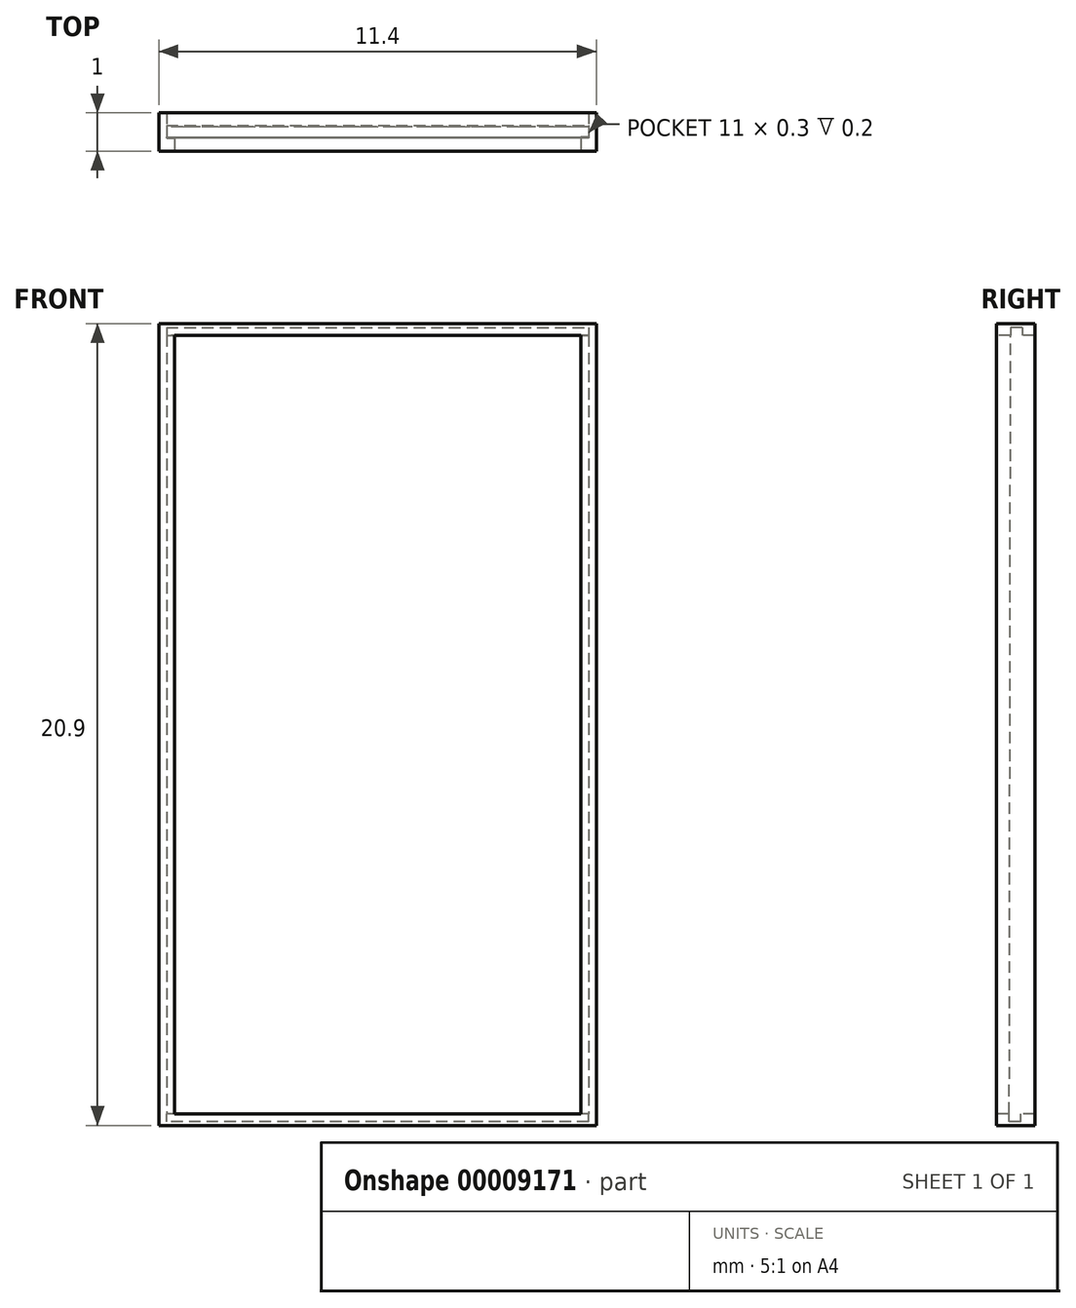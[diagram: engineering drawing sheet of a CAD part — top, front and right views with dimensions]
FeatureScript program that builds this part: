
annotation { "Feature Type Name" : "Feature", "Feature Type Description" : "" }
export const myFeature = defineFeature(function(context is Context, id is Id, definition is map)
    precondition{}
    {
        {
            var Q0;
            Q0=qCreatedBy(makeId("Front.planeOp"),FACE);
            var sketch = newSketch(context, id + "F0", { "sketchPlane" : qUnion([Q0])});
            skLineSegment(sketch, "E0.rect.bottom", {"start": v(5.7, 10.45) * mm, "end": v(-5.7, 10.45) * mm});
            skLineSegment(sketch, "E0.rect.top", {"start": v(5.7, -10.45) * mm, "end": v(-5.7, -10.45) * mm});
            skLineSegment(sketch, "E0.rect.left", {"start": v(5.7, 10.45) * mm, "end": v(5.7, -10.45) * mm});
            skLineSegment(sketch, "E0.rect.right", {"start": v(-5.7, 10.45) * mm, "end": v(-5.7, -10.45) * mm});
            skPoint(sketch, "E0.rect.middle", {"position": v(0, 0) * mm});
            skSolve(sketch);
        }
        {
            var Q0;
            Q0 = qSketchRegion(id + "F0", true);
            extrude(context, id + "F1", {"entities" : qUnion([Q0]), "oppositeDirection" : true, "depth" : 1 * mm});
        }
        {
            var Q0;
            Q0=makeQuery(id+"F1.opExtrude","CAP_FACE",FACE,{"disambiguationData":[OSD([sQuery(id+"F0.wireOp",EDGE,"E0.rect.bottom"),sQuery(id+"F0.wireOp",EDGE,"E0.rect.top"),sQuery(id+"F0.wireOp",EDGE,"E0.rect.left"),sQuery(id+"F0.wireOp",EDGE,"E0.rect.right")])],"isStart":true});
            var sketch = newSketch(context, id + "F2", { "sketchPlane" : qUnion([Q0])});
            skLineSegment(sketch, "E1.rect.bottom", {"start": v(5.3, 10.15) * mm, "end": v(-5.3, 10.15) * mm});
            skLineSegment(sketch, "E1.rect.top", {"start": v(5.3, -10.15) * mm, "end": v(-5.3, -10.15) * mm});
            skLineSegment(sketch, "E1.rect.left", {"start": v(5.3, 10.15) * mm, "end": v(5.3, -10.15) * mm});
            skLineSegment(sketch, "E1.rect.right", {"start": v(-5.3, 10.15) * mm, "end": v(-5.3, -10.15) * mm});
            skPoint(sketch, "E1.rect.middle", {"position": v(0, 0) * mm});
            skSolve(sketch);
        }
        {
            var Q0;
            Q0 = qSketchRegion(id + "F2", true);
            extrude(context, id + "F3", {"entities" : qUnion([Q0]), "operationType" : NewBodyOperationType.REMOVE, "oppositeDirection" : true, "depth" : 25 * mm});
        }
        {
            var Q0;
            Q0=makeQuery(id+"F3.boolean.opBoolean","COPY",FACE,{"derivedFrom":makeQuery(id+"F3.opExtrude","SWEPT_FACE",FACE,{"disambiguationData":[OSD([sQuery(id+"F2.wireOp",EDGE,"E1.rect.top")])]})});
            var sketch = newSketch(context, id + "F4", { "sketchPlane" : qUnion([Q0])});
            skLineSegment(sketch, "E2.rect.bottom", {"start": v(5.3, 0.33) * mm, "end": v(-5.3, 0.33) * mm});
            skLineSegment(sketch, "E2.rect.top", {"start": v(5.3, 0.63) * mm, "end": v(-5.3, 0.63) * mm});
            skLineSegment(sketch, "E2.rect.left", {"start": v(5.3, 0.33) * mm, "end": v(5.3, 0.63) * mm});
            skLineSegment(sketch, "E2.rect.right", {"start": v(-5.3, 0.33) * mm, "end": v(-5.3, 0.63) * mm});
            skPoint(sketch, "E2.rect.middle", {"position": v(0, 0.48) * mm});
            skSolve(sketch);
        }
        {
            var Q0;
            Q0 = qSketchRegion(id + "F4", true);
            extrude(context, id + "F5", {"entities" : qUnion([Q0]), "operationType" : NewBodyOperationType.REMOVE, "oppositeDirection" : true, "depth" : 0.2 * mm});
        }
        {
            var Q0;
            Q0=makeQuery(id+"F3.boolean.opBoolean","COPY",FACE,{"derivedFrom":makeQuery(id+"F3.opExtrude","SWEPT_FACE",FACE,{"disambiguationData":[OSD([sQuery(id+"F2.wireOp",EDGE,"E1.rect.bottom")])]})});
            var sketch = newSketch(context, id + "F6", { "sketchPlane" : qUnion([Q0])});
            skLineSegment(sketch, "E3.rect.bottom", {"start": v(-5.3, -0.37) * mm, "end": v(5.3, -0.37) * mm});
            skLineSegment(sketch, "E3.rect.top", {"start": v(-5.3, -0.67) * mm, "end": v(5.3, -0.67) * mm});
            skLineSegment(sketch, "E3.rect.left", {"start": v(-5.3, -0.37) * mm, "end": v(-5.3, -0.67) * mm});
            skLineSegment(sketch, "E3.rect.right", {"start": v(5.3, -0.37) * mm, "end": v(5.3, -0.67) * mm});
            skPoint(sketch, "E3.rect.middle", {"position": v(0, -0.52) * mm});
            skSolve(sketch);
        }
        {
            var Q0;
            Q0 = qSketchRegion(id + "F6", true);
            extrude(context, id + "F7", {"entities" : qUnion([Q0]), "operationType" : NewBodyOperationType.REMOVE, "oppositeDirection" : true, "depth" : 0.2 * mm});
        }
        {
            var Q0;
            Q0=makeQuery(id+"F7.boolean.opBoolean","MERGE",FACE,{"derivedFrom":[makeQuery(id+"F5.boolean.opBoolean","MERGE",FACE,{"derivedFrom":[makeQuery(id+"F3.boolean.opBoolean","COPY",FACE,{"derivedFrom":makeQuery(id+"F3.opExtrude","SWEPT_FACE",FACE,{"disambiguationData":[OSD([sQuery(id+"F2.wireOp",EDGE,"E1.rect.right")])]})}),makeQuery(id+"F5.opExtrude","SWEPT_FACE",FACE,{"disambiguationData":[OSD([sQuery(id+"F4.wireOp",EDGE,"E2.rect.right")])]})]}),makeQuery(id+"F7.opExtrude","SWEPT_FACE",FACE,{"disambiguationData":[OSD([sQuery(id+"F6.wireOp",EDGE,"E3.rect.left")])]})]});
            var sketch = newSketch(context, id + "F8", { "sketchPlane" : qUnion([Q0])});
            skLineSegment(sketch, "E4", {"start": v(0.33, -10.15) * mm, "end": v(0.37, 10.15) * mm});
            skLineSegment(sketch, "E5", {"start": v(0.67, 10.15) * mm, "end": v(0.63, -10.15) * mm});
            skSolve(sketch);
        }
        {
            var Q0;
            Q0=makeQuery(id+"F8.imprint","IMPRINT",FACE,{"disambiguationData":[TD([[makeQuery(id+"F8.imprint","IMPRINT",EDGE,{"derivedFrom":sQuery(id+"F8.wireOp",EDGE,"E4")}),-1.0]])]});
            extrude(context, id + "F9", {"entities" : qUnion([Q0]), "operationType" : NewBodyOperationType.REMOVE, "oppositeDirection" : true, "depth" : 0.2 * mm});
        }
        {
            var Q0;
            Q0=makeQuery(id+"F7.boolean.opBoolean","MERGE",FACE,{"derivedFrom":[makeQuery(id+"F5.boolean.opBoolean","MERGE",FACE,{"derivedFrom":[makeQuery(id+"F3.boolean.opBoolean","COPY",FACE,{"derivedFrom":makeQuery(id+"F3.opExtrude","SWEPT_FACE",FACE,{"disambiguationData":[OSD([sQuery(id+"F2.wireOp",EDGE,"E1.rect.left")])]})}),makeQuery(id+"F5.opExtrude","SWEPT_FACE",FACE,{"disambiguationData":[OSD([sQuery(id+"F4.wireOp",EDGE,"E2.rect.left")])]})]}),makeQuery(id+"F7.opExtrude","SWEPT_FACE",FACE,{"disambiguationData":[OSD([sQuery(id+"F6.wireOp",EDGE,"E3.rect.right")])]})]});
            var sketch = newSketch(context, id + "F10", { "sketchPlane" : qUnion([Q0])});
            skLineSegment(sketch, "E6", {"start": v(-0.33, -10.15) * mm, "end": v(-0.37, 10.15) * mm});
            skLineSegment(sketch, "E7", {"start": v(-0.67, 10.15) * mm, "end": v(-0.63, -10.15) * mm});
            skSolve(sketch);
        }
        {
            var Q0;
            Q0=makeQuery(id+"F10.imprint","IMPRINT",FACE,{"disambiguationData":[TD([[makeQuery(id+"F10.imprint","IMPRINT",EDGE,{"derivedFrom":sQuery(id+"F10.wireOp",EDGE,"E6")}),1.0]])]});
            extrude(context, id + "F11", {"entities" : qUnion([Q0]), "operationType" : NewBodyOperationType.REMOVE, "oppositeDirection" : true, "depth" : 0.2 * mm});
        }
        {
            var Q0;
            {var subQ0=sQuery(id+"F2.wireOp",EDGE,"E1.rect.left");var subQ1=sQuery(id+"F4.wireOp",EDGE,"E2.rect.left");var subQ2=sQuery(id+"F6.wireOp",EDGE,"E3.rect.right");var subQ6=sQuery(id+"F4.wireOp",EDGE,"E2.rect.top");Q0=makeQuery(id+"F11.boolean.opBoolean","SPLIT",FACE,{"disambiguationData":[TD([makeQuery(id+"F5.boolean.opBoolean","COPY",FACE,{"derivedFrom":makeQuery(id+"F5.opExtrude","SWEPT_FACE",FACE,{"disambiguationData":[OSD([subQ6])]})})])],"derivedFrom":makeQuery(id+"F7.boolean.opBoolean","MERGE",FACE,{"derivedFrom":[makeQuery(id+"F5.boolean.opBoolean","MERGE",FACE,{"derivedFrom":[makeQuery(id+"F3.boolean.opBoolean","COPY",FACE,{"derivedFrom":makeQuery(id+"F3.opExtrude","SWEPT_FACE",FACE,{"disambiguationData":[OSD([subQ0])]})}),makeQuery(id+"F5.opExtrude","SWEPT_FACE",FACE,{"disambiguationData":[OSD([subQ1])]})]}),makeQuery(id+"F7.opExtrude","SWEPT_FACE",FACE,{"disambiguationData":[OSD([subQ2])]})]})});}
            extrude(context, id + "F12", {"entities" : qUnion([Q0]), "operationType" : NewBodyOperationType.REMOVE, "oppositeDirection" : true, "depth" : 0.2 * mm});
        }
        {
            var Q0;
            {var subQ0=sQuery(id+"F2.wireOp",EDGE,"E1.rect.right");var subQ1=sQuery(id+"F4.wireOp",EDGE,"E2.rect.right");var subQ2=sQuery(id+"F6.wireOp",EDGE,"E3.rect.left");var subQ6=sQuery(id+"F4.wireOp",EDGE,"E2.rect.top");Q0=makeQuery(id+"F9.boolean.opBoolean","SPLIT",FACE,{"disambiguationData":[TD([makeQuery(id+"F5.boolean.opBoolean","COPY",FACE,{"derivedFrom":makeQuery(id+"F5.opExtrude","SWEPT_FACE",FACE,{"disambiguationData":[OSD([subQ6])]})})])],"derivedFrom":makeQuery(id+"F7.boolean.opBoolean","MERGE",FACE,{"derivedFrom":[makeQuery(id+"F5.boolean.opBoolean","MERGE",FACE,{"derivedFrom":[makeQuery(id+"F3.boolean.opBoolean","COPY",FACE,{"derivedFrom":makeQuery(id+"F3.opExtrude","SWEPT_FACE",FACE,{"disambiguationData":[OSD([subQ0])]})}),makeQuery(id+"F5.opExtrude","SWEPT_FACE",FACE,{"disambiguationData":[OSD([subQ1])]})]}),makeQuery(id+"F7.opExtrude","SWEPT_FACE",FACE,{"disambiguationData":[OSD([subQ2])]})]})});}
            extrude(context, id + "F13", {"entities" : qUnion([Q0]), "operationType" : NewBodyOperationType.REMOVE, "oppositeDirection" : true, "depth" : 0.2 * mm});
        }
    });
